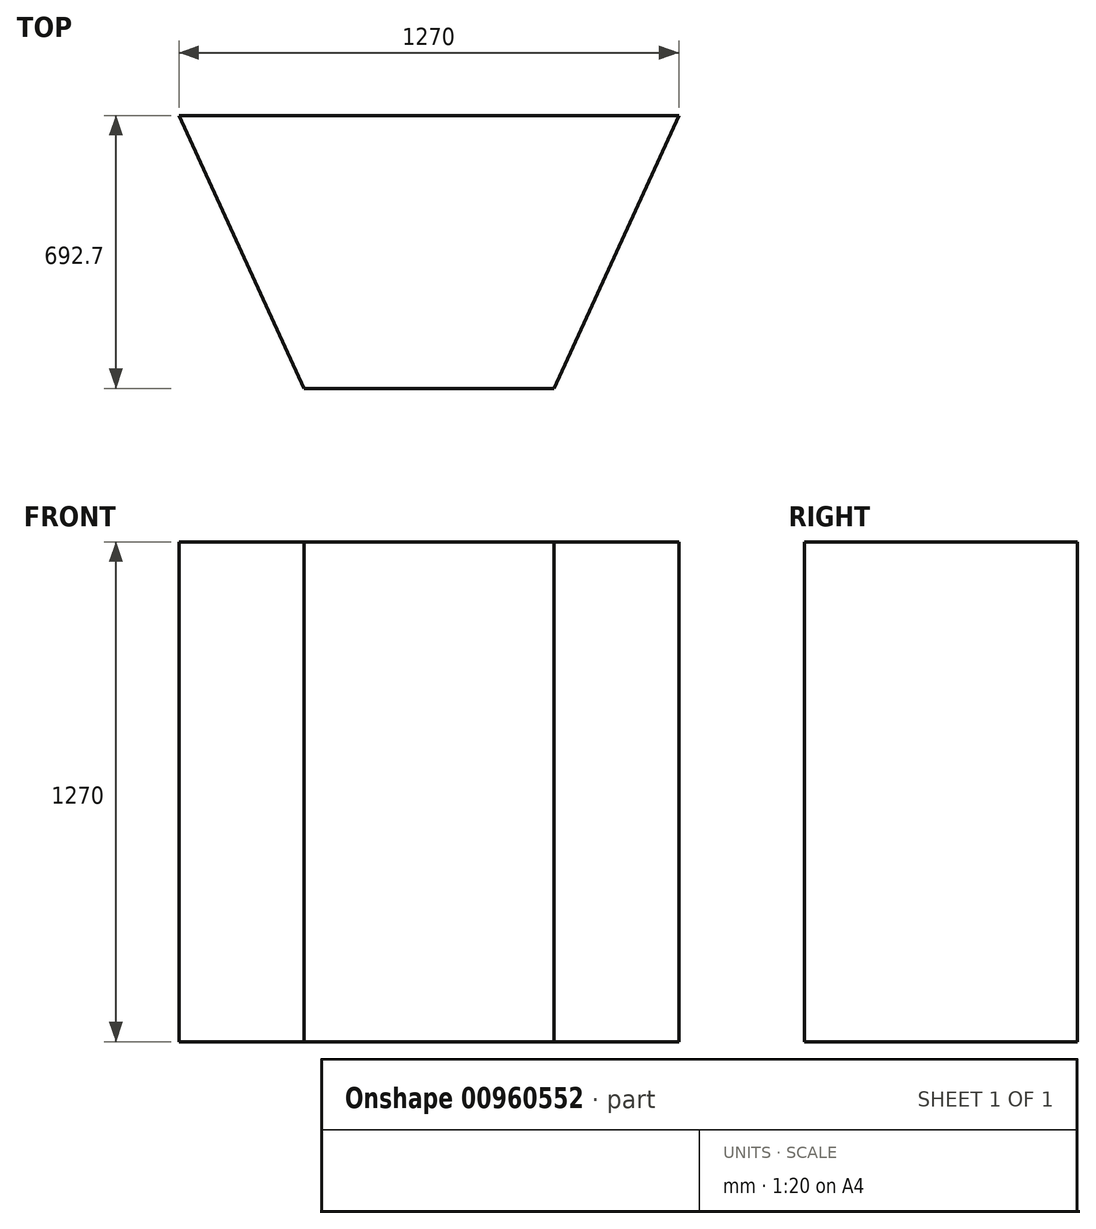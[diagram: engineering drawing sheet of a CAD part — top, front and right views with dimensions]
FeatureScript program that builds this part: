
annotation { "Feature Type Name" : "Feature", "Feature Type Description" : "" }
export const myFeature = defineFeature(function(context is Context, id is Id, definition is map)
    precondition{}
    {
        {
            var Q0;
            Q0=qCreatedBy(makeId("Top.planeOp"),FACE);
            var sketch = newSketch(context, id + "F0", { "sketchPlane" : qUnion([Q0])});
            skLineSegment(sketch, "E0", {"start": v(-619.54, 402.6) * mm, "end": v(650.46, 402.6) * mm});
            skLineSegment(sketch, "E1", {"start": v(650.46, 402.6) * mm, "end": v(332.96, -290.11) * mm});
            skLineSegment(sketch, "E2", {"start": v(332.96, -290.11) * mm, "end": v(-302.04, -290.11) * mm});
            skLineSegment(sketch, "E3", {"start": v(-302.04, -290.11) * mm, "end": v(-619.54, 402.6) * mm});
            skSolve(sketch);
        }
        {
            var Q0;
            Q0=makeQuery(id+"F0.imprint","IMPRINT",FACE,{"disambiguationData":[TD([[makeQuery(id+"F0.imprint","IMPRINT",EDGE,{"derivedFrom":sQuery(id+"F0.wireOp",EDGE,"E0")}),-1.0]])]});
            extrude(context, id + "F1", {"entities" : qUnion([Q0]), "depth" : 1270 * mm, "offsetDistance" : 25.4 * mm});
        }
    });
